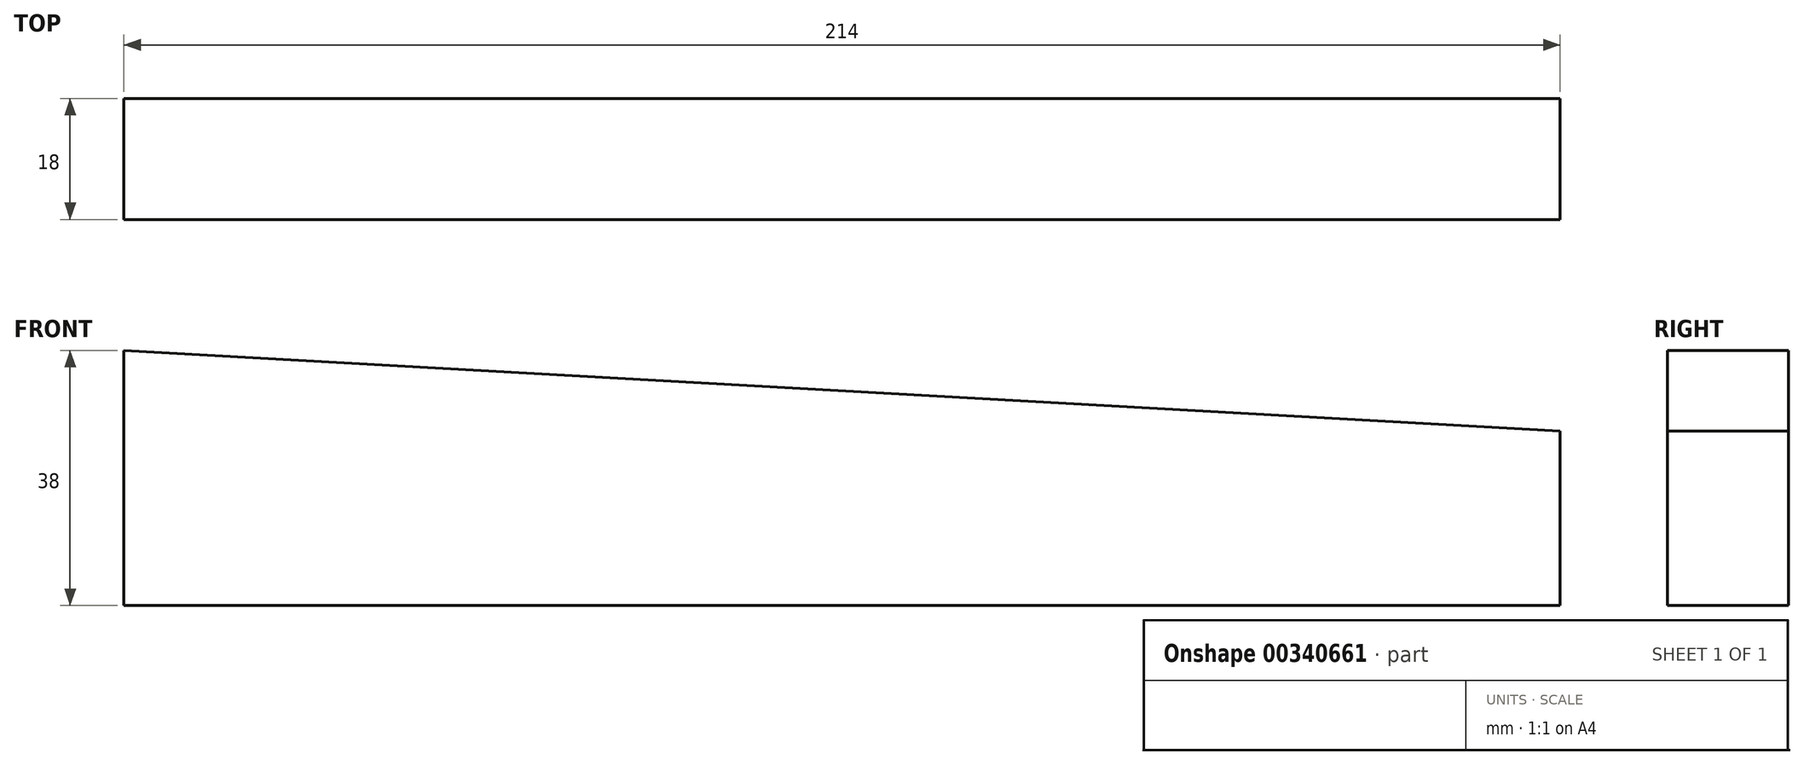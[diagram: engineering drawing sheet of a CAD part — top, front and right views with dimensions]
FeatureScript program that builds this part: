
annotation { "Feature Type Name" : "Feature", "Feature Type Description" : "" }
export const myFeature = defineFeature(function(context is Context, id is Id, definition is map)
    precondition{}
    {
        {
            var Q0;
            Q0=qCreatedBy(makeId("Front.planeOp"),FACE);
            var sketch = newSketch(context, id + "F0", { "sketchPlane" : qUnion([Q0])});
            skLineSegment(sketch, "E0.top", {"start": v(-94.9, -37.3) * mm, "end": v(119.1, -37.3) * mm});
            skLineSegment(sketch, "E0.left", {"start": v(-94.9, 0.7) * mm, "end": v(-94.9, -37.3) * mm});
            skLineSegment(sketch, "E0.right", {"start": v(119.1, -11.3) * mm, "end": v(119.1, -37.3) * mm});
            skLineSegment(sketch, "E1", {"start": v(-94.9, 0.7) * mm, "end": v(119.1, -11.3) * mm});
            skPoint(sketch, "E2.orphan", {"position": v(119.1, 0.7) * mm});
            skSolve(sketch);
        }
        {
            var Q0;
            Q0=makeQuery(id+"F0.imprint","IMPRINT",FACE,{"disambiguationData":[TD([[makeQuery(id+"F0.imprint","IMPRINT",EDGE,{"derivedFrom":sQuery(id+"F0.wireOp",EDGE,"E0.top")}),1.0]])]});
            extrude(context, id + "F1", {"entities" : qUnion([Q0]), "depth" : 18 * mm});
        }
    });
